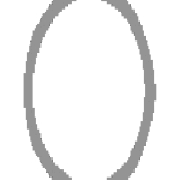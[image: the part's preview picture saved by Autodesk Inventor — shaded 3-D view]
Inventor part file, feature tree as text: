
AUTODESK INVENTOR PART (.ipt)
format: ipt  version: 2021 (Build 250183000, 183)  size: 114,688 bytes
history: native  units: in
note: dims shown in document units (in); Inventor stores cm internally (conversion verified against a paired STEP export)
features: other x4, sketch x3, plane x1
ambient origin geometry x8: Origin, YZ Plane, XZ Plane, XY Plane, X Axis, Y Axis, Z Axis, Center Point
bodies: Solid1 (feature_tree), Body (feature_tree)
feature tree (8):
  other  "Driven Length"
  other  "Frame Generator"
  other  "Start Plane"
  other  "End Plane"
  sketch  "Sketch"  dims[d2=1.5435in d4=-0.0in d5=1.5435in d6=0.12in d7=0.0in d8=90.0deg d9=1.5435in]
  sketch  "Sketch2"  dims[d0=1.0in]
  plane  "Work Plane3"
  sketch  "Sketch3"  dims[d1=0.065in]
